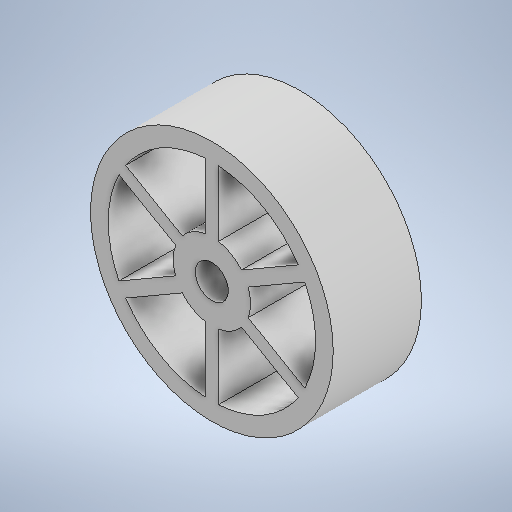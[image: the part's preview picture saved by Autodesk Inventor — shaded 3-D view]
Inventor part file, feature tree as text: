
AUTODESK INVENTOR PART (.ipt)
format: ipt  version: 2025.3 (Build 293356030, 356C)  size: 276,992 bytes
history: native  units: mm
features: sketch x2, other x1, extrude x1, pattern_circular x1
ambient origin geometry x8: Origin, YZ Plane, XZ Plane, XY Plane, X Axis, Y Axis, Z Axis, Center Point
bodies: Body1 (feature_tree)
feature tree (5):
  other  "ソリッド1"
  extrude  "スポーク"  Depth=1.6mm
  pattern_circular  "円形状パターン1"  [2 undecoded]
  sketch  "スケッチ1"
  sketch  "スケッチ2"
note: 2 required parameter values undecoded (feature->parameter linkage not recoverable at this tier; creation-order binding heuristic only, values carry confidence <= 0.55)
